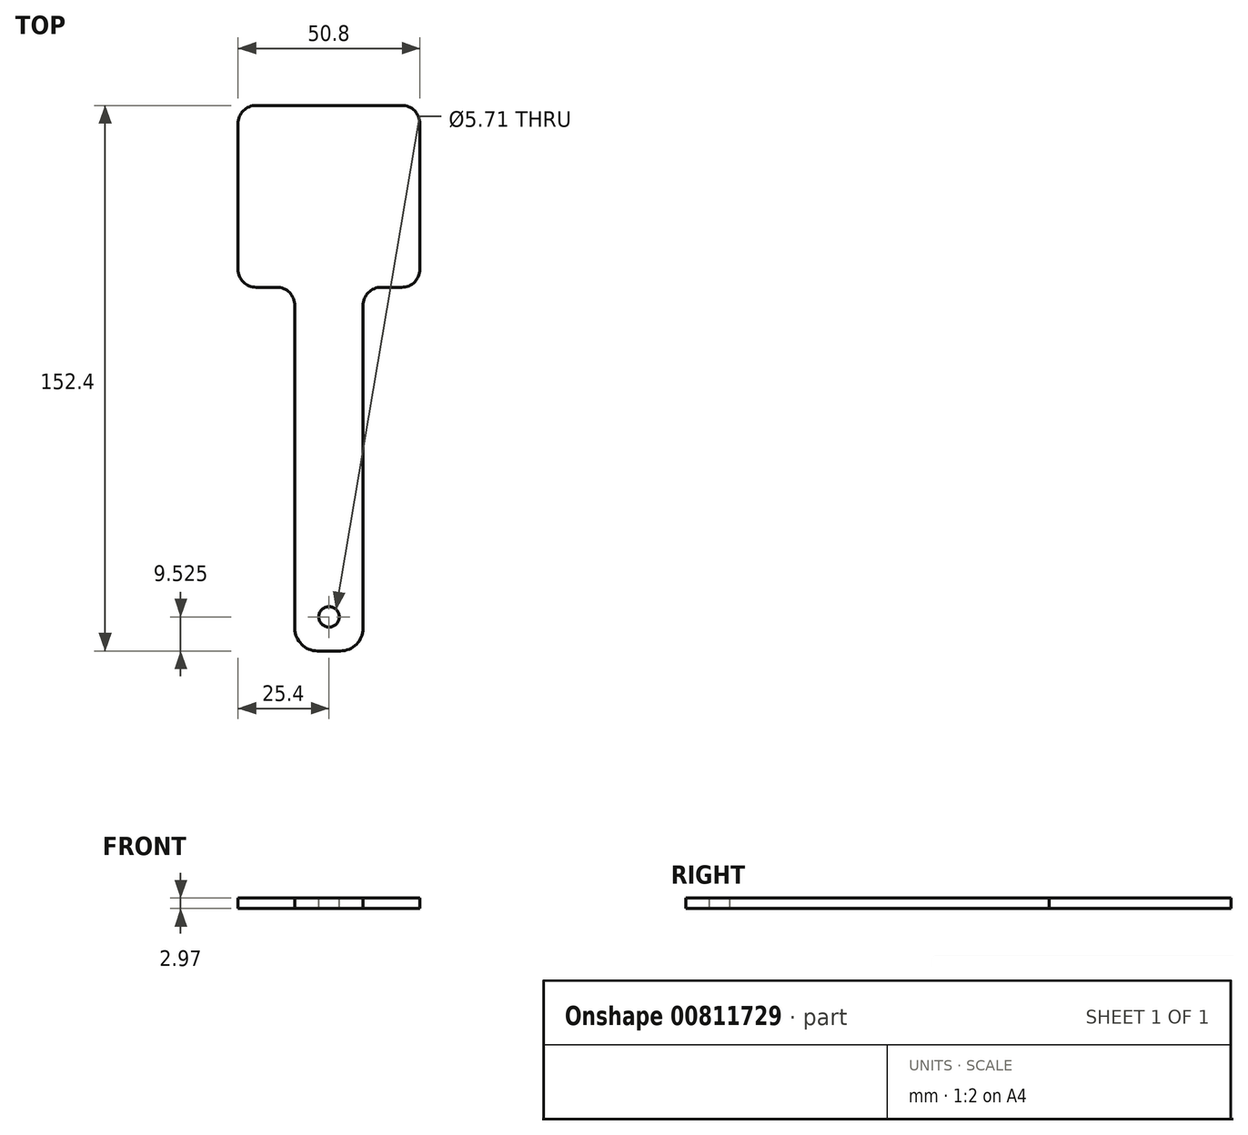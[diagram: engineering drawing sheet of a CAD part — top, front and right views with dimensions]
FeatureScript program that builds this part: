
annotation { "Feature Type Name" : "Feature", "Feature Type Description" : "" }
export const myFeature = defineFeature(function(context is Context, id is Id, definition is map)
    precondition{}
    {
        {
            var Q0;
            Q0=qCreatedBy(makeId("Top.planeOp"),FACE);
            var sketch = newSketch(context, id + "F0", { "sketchPlane" : qUnion([Q0])});
            skLineSegment(sketch, "E0.bottom", {"start": v(9.53, 76.2) * mm, "end": v(-9.52, 76.2) * mm});
            skLineSegment(sketch, "E0.top", {"start": v(9.52, -76.2) * mm, "end": v(-9.53, -76.2) * mm});
            skLineSegment(sketch, "E0.left", {"start": v(9.53, 76.2) * mm, "end": v(9.52, -76.2) * mm});
            skLineSegment(sketch, "E0.right", {"start": v(-9.52, 76.2) * mm, "end": v(-9.53, -76.2) * mm});
            skPoint(sketch, "E0.middle", {"position": v(0, 0) * mm});
            skSolve(sketch);
        }
        {
            var Q0;
            Q0 = qSketchRegion(id + "F0", true);
            extrude(context, id + "F1", {"entities" : qUnion([Q0]), "depth" : 2.97 * mm, "offsetDistance" : 25.4 * mm});
        }
        {
            var Q0;
            Q0=makeQuery(id+"F1.opExtrude","SWEPT_EDGE",EDGE,{"disambiguationData":[OSD([sQuery(id+"F0.wireOp",EDGE,"E0.top"),sQuery(id+"F0.wireOp",EDGE,"E0.left")])]});
            var Q1;
            Q1=makeQuery(id+"F1.opExtrude","SWEPT_EDGE",EDGE,{"disambiguationData":[OSD([sQuery(id+"F0.wireOp",EDGE,"E0.top"),sQuery(id+"F0.wireOp",EDGE,"E0.right")])]});
            fillet(context, id + "F2", {"entities" : qUnion([Q0, Q1]), "radius" : 6.35 * mm, "tangentPropagation" : true, "allowEdgeOverflow" : false});
        }
        {
            var Q0;
            Q0=makeQuery(id+"F1.opExtrude","CAP_FACE",FACE,{"disambiguationData":[OSD([sQuery(id+"F0.wireOp",EDGE,"E0.bottom"),sQuery(id+"F0.wireOp",EDGE,"E0.top"),sQuery(id+"F0.wireOp",EDGE,"E0.left"),sQuery(id+"F0.wireOp",EDGE,"E0.right")])],"isStart":false});
            var sketch = newSketch(context, id + "F3", { "sketchPlane" : qUnion([Q0])});
            skCircle(sketch, "E1", {"center": v(0, -66.67) * mm, "radius": 2.86 * mm});
            skSolve(sketch);
        }
        {
            var Q0;
            Q0 = qSketchRegion(id + "F3", true);
            extrude(context, id + "F4", {"entities" : qUnion([Q0]), "operationType" : NewBodyOperationType.REMOVE, "oppositeDirection" : true, "depth" : 25.4 * mm, "offsetDistance" : 25.4 * mm});
        }
        {
            var Q0;
            Q0=makeQuery(id+"F1.opExtrude","CAP_FACE",FACE,{"disambiguationData":[OSD([sQuery(id+"F0.wireOp",EDGE,"E0.bottom"),sQuery(id+"F0.wireOp",EDGE,"E0.top"),sQuery(id+"F0.wireOp",EDGE,"E0.left"),sQuery(id+"F0.wireOp",EDGE,"E0.right")])],"isStart":false});
            var sketch = newSketch(context, id + "F5", { "sketchPlane" : qUnion([Q0])});
            skPoint(sketch, "E2.firstSnap0", {"position": v(0, 76.2) * mm});
            skLineSegment(sketch, "E2.bottom", {"start": v(-25.4, 76.2) * mm, "end": v(25.4, 76.2) * mm});
            skLineSegment(sketch, "E2.top", {"start": v(-25.4, 25.4) * mm, "end": v(25.4, 25.4) * mm});
            skLineSegment(sketch, "E2.left", {"start": v(-25.4, 76.2) * mm, "end": v(-25.4, 25.4) * mm});
            skLineSegment(sketch, "E2.right", {"start": v(25.4, 76.2) * mm, "end": v(25.4, 25.4) * mm});
            skSolve(sketch);
        }
        {
            var Q0;
            Q0 = qSketchRegion(id + "F5", true);
            extrude(context, id + "F6", {"entities" : qUnion([Q0]), "operationType" : NewBodyOperationType.ADD, "oppositeDirection" : true, "depth" : 2.97 * mm, "offsetDistance" : 25.4 * mm});
        }
        {
            var Q0;
            Q0=makeQuery(id+"F6.boolean.opBoolean","INTERSECT",EDGE,{"derivedFrom":[makeQuery(id+"F1.opExtrude","SWEPT_FACE",FACE,{"disambiguationData":[OSD([sQuery(id+"F0.wireOp",EDGE,"E0.left")])]}),makeQuery(id+"F6.opExtrude","SWEPT_FACE",FACE,{"disambiguationData":[OSD([sQuery(id+"F5.wireOp",EDGE,"E2.top")])]})]});
            var Q1;
            Q1=makeQuery(id+"F6.opExtrude","SWEPT_EDGE",EDGE,{"disambiguationData":[OSD([sQuery(id+"F5.wireOp",EDGE,"E2.top"),sQuery(id+"F5.wireOp",EDGE,"E2.right")])]});
            var Q2;
            Q2=makeQuery(id+"F6.boolean.opBoolean","INTERSECT",EDGE,{"derivedFrom":[makeQuery(id+"F1.opExtrude","SWEPT_FACE",FACE,{"disambiguationData":[OSD([sQuery(id+"F0.wireOp",EDGE,"E0.right")])]}),makeQuery(id+"F6.opExtrude","SWEPT_FACE",FACE,{"disambiguationData":[OSD([sQuery(id+"F5.wireOp",EDGE,"E2.top")])]})]});
            var Q3;
            Q3=makeQuery(id+"F6.opExtrude","SWEPT_EDGE",EDGE,{"disambiguationData":[OSD([sQuery(id+"F5.wireOp",EDGE,"E2.top"),sQuery(id+"F5.wireOp",EDGE,"E2.left")])]});
            var Q4;
            Q4=makeQuery(id+"F6.opExtrude","SWEPT_EDGE",EDGE,{"disambiguationData":[OSD([sQuery(id+"F5.wireOp",EDGE,"E2.bottom"),sQuery(id+"F5.wireOp",EDGE,"E2.right")])]});
            var Q5;
            Q5=makeQuery(id+"F6.opExtrude","SWEPT_EDGE",EDGE,{"disambiguationData":[OSD([sQuery(id+"F5.wireOp",EDGE,"E2.bottom"),sQuery(id+"F5.wireOp",EDGE,"E2.left")])]});
            fillet(context, id + "F7", {"entities" : qUnion([Q0, Q1, Q2, Q3, Q4, Q5]), "radius" : 5.08 * mm, "tangentPropagation" : true, "allowEdgeOverflow" : false});
        }
    });
